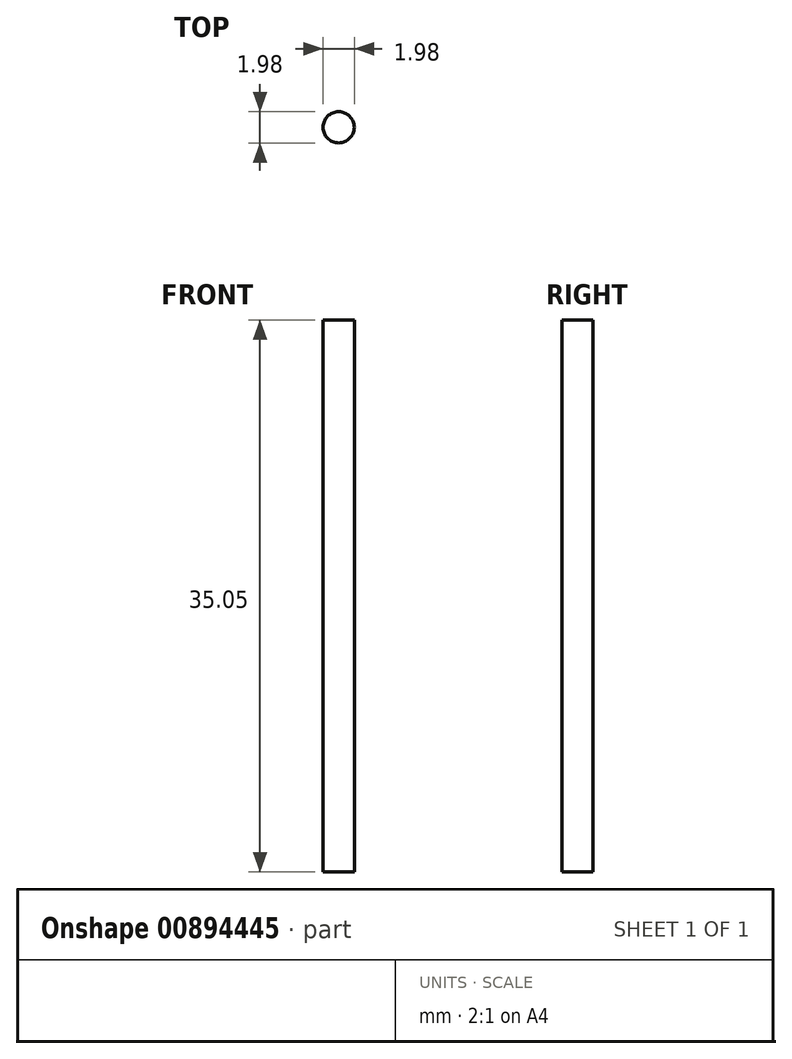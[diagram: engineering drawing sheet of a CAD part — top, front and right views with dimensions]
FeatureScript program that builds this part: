
annotation { "Feature Type Name" : "Feature", "Feature Type Description" : "" }
export const myFeature = defineFeature(function(context is Context, id is Id, definition is map)
    precondition{}
    {
        {
            var Q0;
            Q0=qCreatedBy(makeId("Top.planeOp"),FACE);
            var sketch = newSketch(context, id + "F0", { "sketchPlane" : qUnion([Q0])});
            skCircle(sketch, "E0", {"center": v(0, 0) * mm, "radius": 1 * mm});
            skSolve(sketch);
        }
        {
            var Q0;
            Q0=makeQuery(id+"F0.imprint","IMPRINT",FACE,{"disambiguationData":[TD([[makeQuery(id+"F0.imprint","IMPRINT",EDGE,{"derivedFrom":sQuery(id+"F0.wireOp",EDGE,"E0")}),1.0]])]});
            extrude(context, id + "F1", {"entities" : qUnion([Q0]), "depth" : 35.05 * mm, "offsetDistance" : 25.4 * mm});
        }
    });
